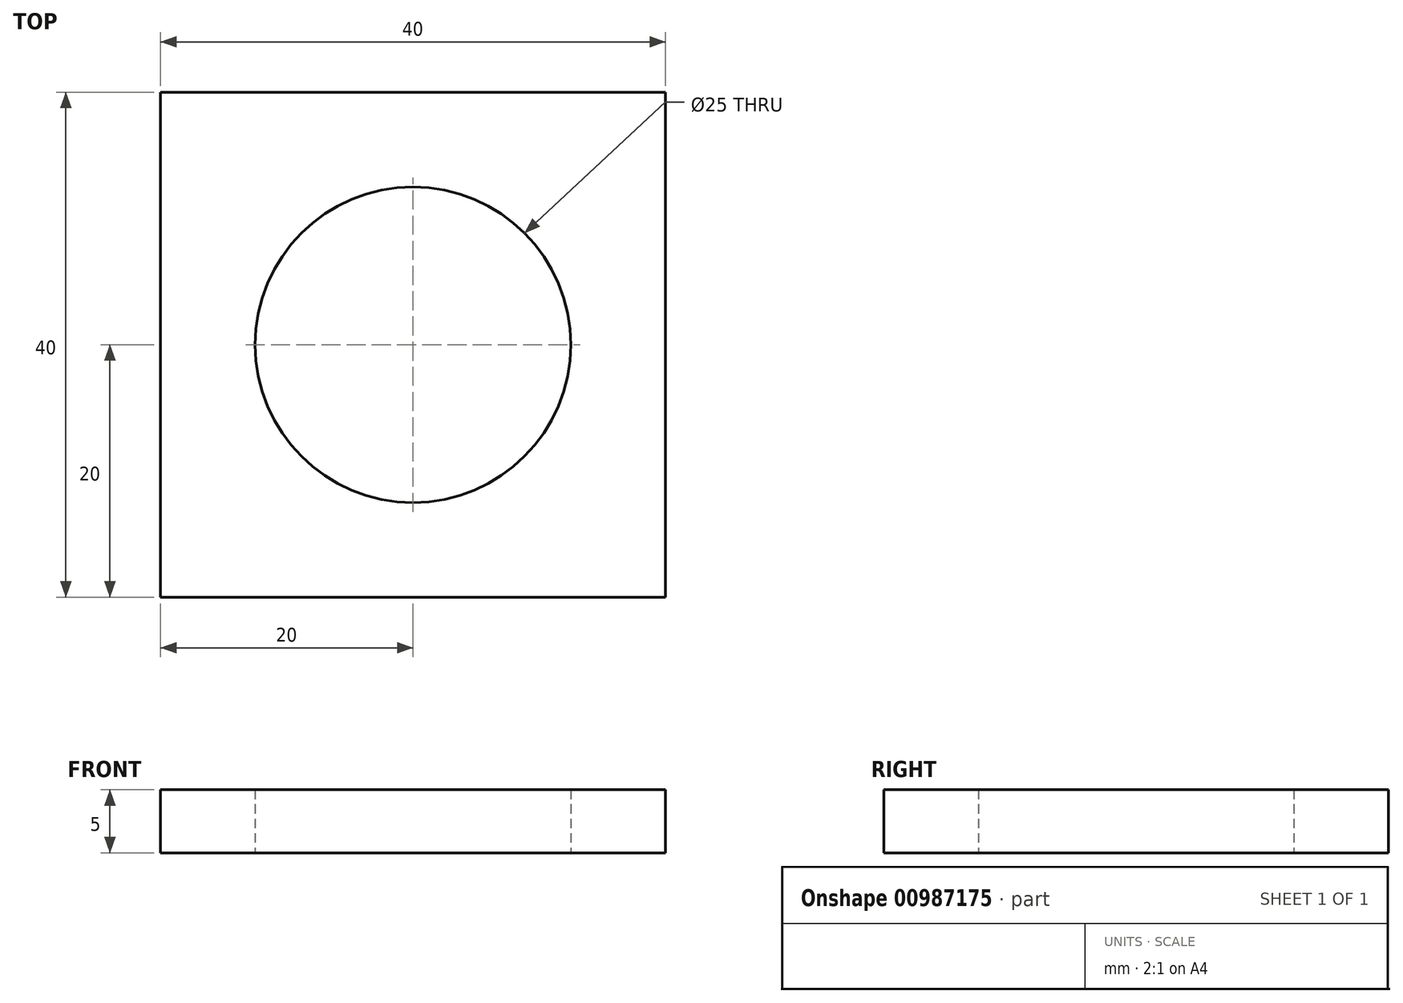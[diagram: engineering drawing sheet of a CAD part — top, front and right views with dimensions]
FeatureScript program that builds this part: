
annotation { "Feature Type Name" : "Feature", "Feature Type Description" : "" }
export const myFeature = defineFeature(function(context is Context, id is Id, definition is map)
    precondition{}
    {
        {
            var Q0;
            Q0=qCreatedBy(makeId("Top.planeOp"),FACE);
            var sketch = newSketch(context, id + "F0", { "sketchPlane" : qUnion([Q0])});
            skCircle(sketch, "E0", {"center": v(0, 0) * mm, "radius": 12.5 * mm});
            skLineSegment(sketch, "E1", {"start": v(-20, 0) * mm, "end": v(-20, 20) * mm});
            skLineSegment(sketch, "E2", {"start": v(-20, 20) * mm, "end": v(20, 20) * mm});
            skLineSegment(sketch, "E3", {"start": v(20, 20) * mm, "end": v(20, -20) * mm});
            skLineSegment(sketch, "E4", {"start": v(20, -20) * mm, "end": v(-20, -20) * mm});
            skLineSegment(sketch, "E5", {"start": v(-20, 0) * mm, "end": v(-20, -20) * mm});
            skSolve(sketch);
        }
        {
            var Q0;
            Q0 = qSketchRegion(id + "F0", true);
            extrude(context, id + "F1", {"entities" : qUnion([Q0]), "depth" : 5 * mm, "offsetDistance" : 25 * mm});
        }
    });
